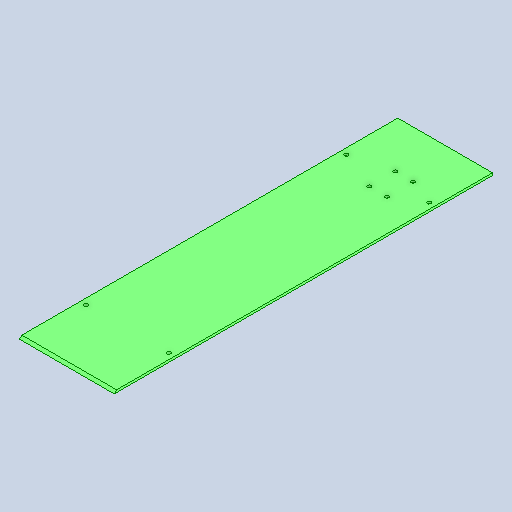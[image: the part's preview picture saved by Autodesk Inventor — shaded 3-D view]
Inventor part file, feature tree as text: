
AUTODESK INVENTOR PART (.ipt)
format: ipt  version: 2022 (Build 260153000, 153)  size: 139,776 bytes
history: native  units: mm
features: sketch x3, hole x2, other x1, extrude x1, chamfer x1
ambient origin geometry x8: Origin, YZ Plane, XZ Plane, XY Plane, X Axis, Y Axis, Z Axis, Center Point
bodies: Body1 (feature_tree)
feature tree (8):
  other  "ソリッド1"
  extrude  "押し出し1"  Depth=319.5mm
  hole  "穴1"  [1 undecoded]
  chamfer  "面取り2"  Distance=2.0mm
  hole  "穴2"  [1 undecoded]
  sketch  "スケッチ1"
  sketch  "スケッチ3"
  sketch  "スケッチ5"
note: 2 required parameter values undecoded (feature->parameter linkage not recoverable at this tier; creation-order binding heuristic only, values carry confidence <= 0.55)
